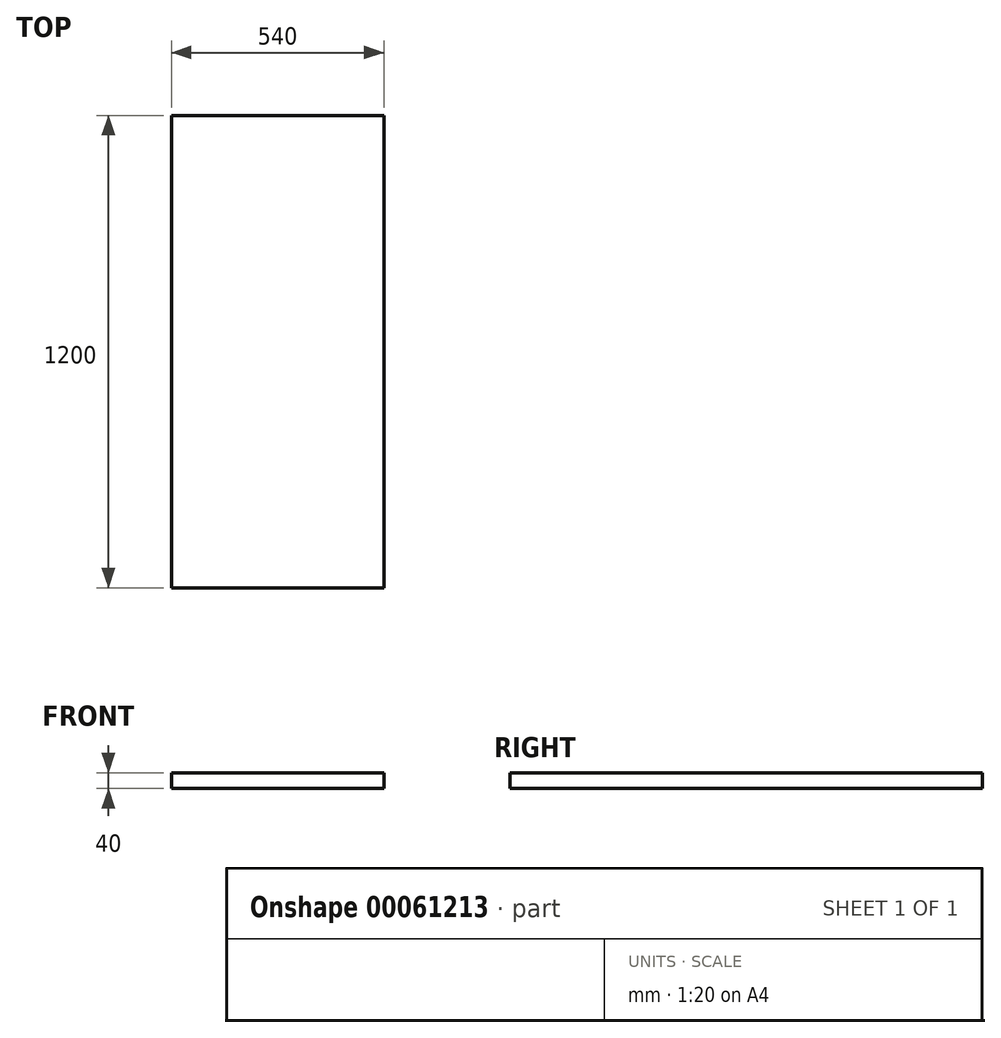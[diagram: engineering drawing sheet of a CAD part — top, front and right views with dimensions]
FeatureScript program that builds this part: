
annotation { "Feature Type Name" : "Feature", "Feature Type Description" : "" }
export const myFeature = defineFeature(function(context is Context, id is Id, definition is map)
    precondition{}
    {
        {
            var Q0;
            Q0=qCreatedBy(makeId("Top.planeOp"),FACE);
            var sketch = newSketch(context, id + "F0", { "sketchPlane" : qUnion([Q0])});
            skLineSegment(sketch, "E0.bottom", {"start": v(0, 1200) * mm, "end": v(540, 1200) * mm});
            skLineSegment(sketch, "E0.top", {"start": v(0, 0) * mm, "end": v(540, 0) * mm});
            skLineSegment(sketch, "E0.left", {"start": v(0, 1200) * mm, "end": v(0, 0) * mm});
            skLineSegment(sketch, "E0.right", {"start": v(540, 1200) * mm, "end": v(540, 0) * mm});
            skSolve(sketch);
        }
        {
            var Q0;
            Q0 = qSketchRegion(id + "F0", true);
            extrude(context, id + "F1", {"entities" : qUnion([Q0]), "depth" : 40 * mm});
        }
    });
